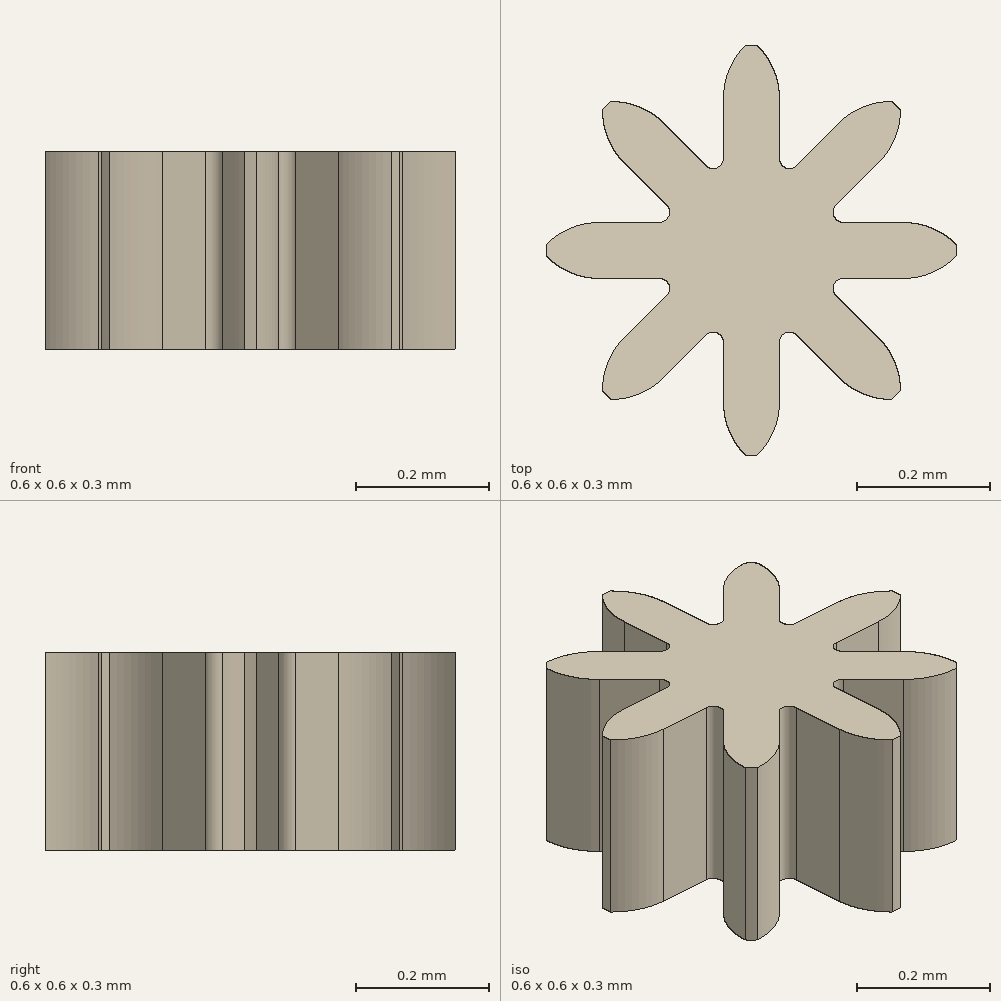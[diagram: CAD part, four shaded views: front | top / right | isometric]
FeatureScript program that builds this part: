
annotation { "Feature Type Name" : "Feature", "Feature Type Description" : "" }
export const myFeature = defineFeature(function(context is Context, id is Id, definition is map)
    precondition{}
    {
        {
            var Q0;
            Q0=qCreatedBy(makeId("Top.planeOp"),FACE);
            var sketch = newSketch(context, id + "F0", { "sketchPlane" : qUnion([Q0])});
            skCircle(sketch, "E0", {"center": v(0, 0) * mm, "radius": 0.14 * mm});
            skArc(sketch, "E1", {"start": v(0.04, 0.24) * mm, "mid": v(-0.14, -0.2) * mm, "end": v(0.21, 0.11) * mm});
            skArc(sketch, "E2", {"start": v(0, 0.3) * mm, "mid": v(-0.12, -0.29) * mm, "end": v(0.21, 0.23) * mm});
            skLineSegment(sketch, "E3", {"start": v(0.04, 0.14) * mm, "end": v(0.04, 0.23) * mm});
            skArc(sketch, "E4", {"start": v(0, 0.3) * mm, "mid": v(0.03, 0.27) * mm, "end": v(0.04, 0.23) * mm});
            skArc(sketch, "E5.1.0", {"start": v(0.21, 0.23) * mm, "mid": v(0.17, 0.22) * mm, "end": v(0.13, 0.2) * mm});
            skLineSegment(sketch, "E5.1.1", {"start": v(0.07, 0.13) * mm, "end": v(0.13, 0.2) * mm});
            skPoint(sketch, "E6.orphan", {"position": v(0.04, 0) * mm});
            skPoint(sketch, "E7.start.orphan", {"position": v(-0.04, 0) * mm});
            skArc(sketch, "E8", {"start": v(0.04, 0.14) * mm, "mid": v(0.05, 0.12) * mm, "end": v(0.07, 0.13) * mm});
            skPoint(sketch, "E9.orphan", {"position": v(-0.04, 0.23) * mm});
            skPoint(sketch, "E10.orphan", {"position": v(0, 0.3) * mm});
            skPoint(sketch, "E11.orphan", {"position": v(0.23, 0.21) * mm});
            skPoint(sketch, "E12.orphan", {"position": v(0.04, 0.13) * mm});
            skPoint(sketch, "E13.orphan", {"position": v(0.06, 0.12) * mm});
            skSolve(sketch);
        }
        {
            var Q0;
            {var subQ4=sQuery(id+"F0.wireOp",EDGE,"E0");Q0=makeQuery(id+"F0.imprint","IMPRINT",FACE,{"disambiguationData":[TD([[makeQuery(id+"F0.imprint","IMPRINT",EDGE,{"derivedFrom":subQ4}),-1.0]])]});}
            var Q1;
            Q1=makeQuery(id+"F0.imprint","IMPRINT",FACE,{"disambiguationData":[TD([[makeQuery(id+"F0.imprint","IMPRINT",EDGE,{"derivedFrom":sQuery(id+"F0.wireOp",EDGE,"E0")}),1.0]])]});
            extrude(context, id + "F1", {"entities" : qUnion([Q0, Q1]), "depth" : 0.3 * mm, "offsetDistance" : 25 * mm});
        }
        {
            var Q0;
            Q0=makeQuery(id+"F1.opExtrude","SWEPT_FACE",FACE,{"disambiguationData":[OSD([sQuery(id+"F0.wireOp",EDGE,"E4")])]});
            var Q1;
            Q1=makeQuery(id+"F1.opExtrude","SWEPT_FACE",FACE,{"disambiguationData":[OSD([sQuery(id+"F0.wireOp",EDGE,"E3")])]});
            var Q2;
            Q2=makeQuery(id+"F1.opExtrude","SWEPT_FACE",FACE,{"disambiguationData":[OSD([sQuery(id+"F0.wireOp",EDGE,"E8")])]});
            var Q3;
            Q3=makeQuery(id+"F1.opExtrude","SWEPT_FACE",FACE,{"disambiguationData":[OSD([sQuery(id+"F0.wireOp",EDGE,"E5.1.1")])]});
            var Q4;
            Q4=makeQuery(id+"F1.opExtrude","SWEPT_FACE",FACE,{"disambiguationData":[OSD([sQuery(id+"F0.wireOp",EDGE,"E5.1.0")])]});
            var Q5;
            Q5=makeQuery(id+"F1.opExtrude","SWEPT_FACE",FACE,{"disambiguationData":[OSD([sQuery(id+"F0.wireOp",EDGE,"E2")])]});
            circularPattern(context, id + "F2", {"patternType" : PatternType.FACE, "faces" : qUnion([Q0, Q1, Q2, Q3, Q4]), "axis" : qUnion([Q5]), "angle" : 360 * degree, "instanceCount" : 8, "equalSpace" : true});
        }
    });
